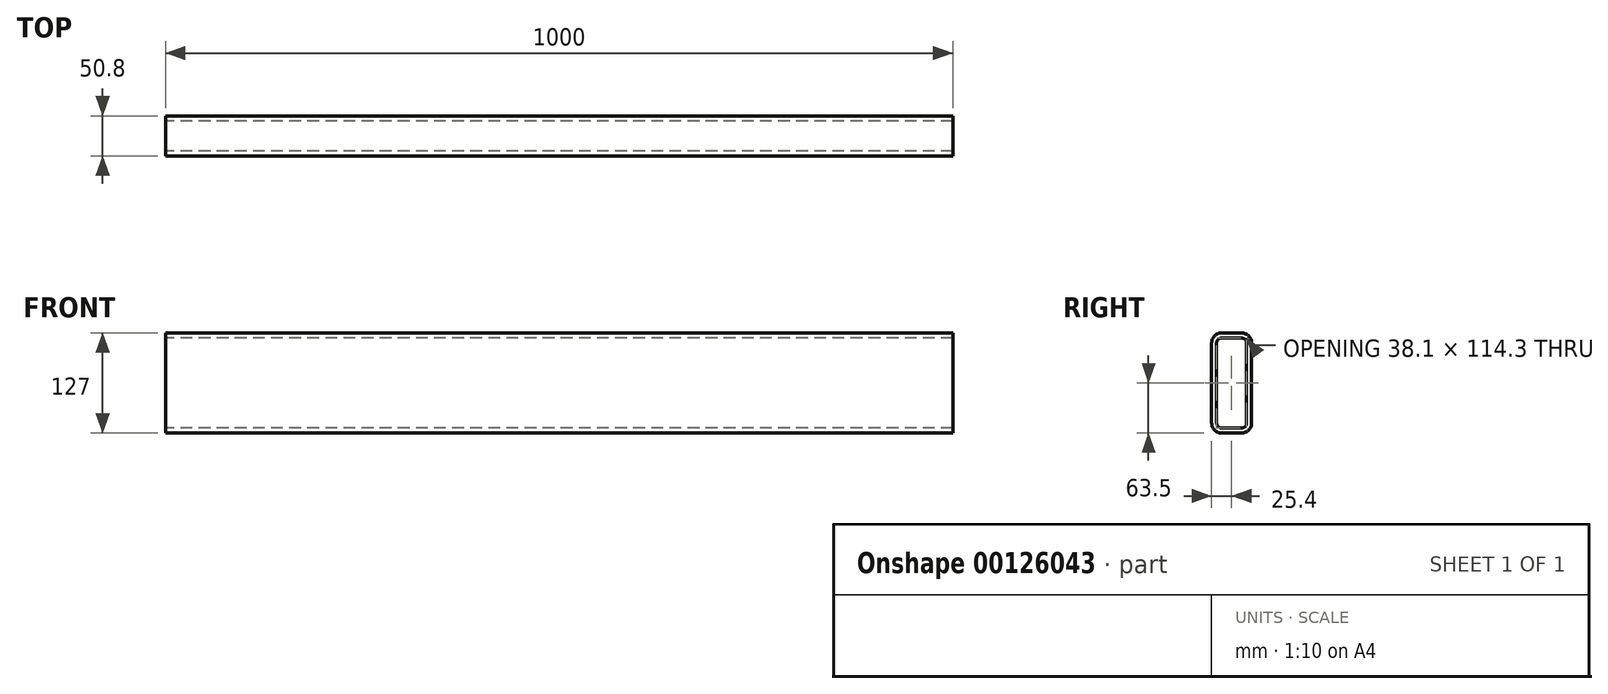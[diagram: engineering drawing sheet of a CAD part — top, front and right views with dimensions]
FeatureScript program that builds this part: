
annotation { "Feature Type Name" : "Feature", "Feature Type Description" : "" }
export const myFeature = defineFeature(function(context is Context, id is Id, definition is map)
    precondition{}
    {
        {
            var Q0;
            Q0=qCreatedBy(makeId("Right.planeOp"),FACE);
            var sketch = newSketch(context, id + "F2", { "sketchPlane" : qUnion([Q0])});
            skLineSegment(sketch, "E0.bottom", {"start": v(12.7, 63.5) * mm, "end": v(-12.7, 63.5) * mm});
            skLineSegment(sketch, "E0.top", {"start": v(12.7, -63.5) * mm, "end": v(-12.7, -63.5) * mm});
            skLineSegment(sketch, "E0.left", {"start": v(25.4, 50.8) * mm, "end": v(25.4, -50.8) * mm});
            skLineSegment(sketch, "E0.right", {"start": v(-25.4, 50.8) * mm, "end": v(-25.4, -50.8) * mm});
            skPoint(sketch, "E0.middle", {"position": v(0, 0) * mm});
            skPoint(sketch, "E1.visualSharp", {"position": v(-25.4, 63.5) * mm});
            skArc(sketch, "E1.filletArc", {"start": v(-12.7, 63.5) * mm, "mid": v(-21.68, 59.78) * mm, "end": v(-25.4, 50.8) * mm});
            skPoint(sketch, "E2.visualSharp", {"position": v(25.4, 63.5) * mm});
            skArc(sketch, "E2.filletArc", {"start": v(25.4, 50.8) * mm, "mid": v(21.68, 59.78) * mm, "end": v(12.7, 63.5) * mm});
            skPoint(sketch, "E3.visualSharp", {"position": v(25.4, -63.5) * mm});
            skArc(sketch, "E3.filletArc", {"start": v(12.7, -63.5) * mm, "mid": v(21.68, -59.78) * mm, "end": v(25.4, -50.8) * mm});
            skPoint(sketch, "E4.visualSharp", {"position": v(-25.4, -63.5) * mm});
            skArc(sketch, "E4.filletArc", {"start": v(-25.4, -50.8) * mm, "mid": v(-21.68, -59.78) * mm, "end": v(-12.7, -63.5) * mm});
            skLineSegment(sketch, "E5.0", {"start": v(12.7, 57.15) * mm, "end": v(-12.7, 57.15) * mm});
            skArc(sketch, "E6.0", {"start": v(19.05, 50.8) * mm, "mid": v(17.2, 55.3) * mm, "end": v(12.7, 57.15) * mm});
            skLineSegment(sketch, "E7.0", {"start": v(19.05, 50.8) * mm, "end": v(19.05, -50.8) * mm});
            skArc(sketch, "E8.0", {"start": v(-12.7, 57.15) * mm, "mid": v(-17.2, 55.3) * mm, "end": v(-19.05, 50.8) * mm});
            skArc(sketch, "E8.1", {"start": v(12.7, -57.15) * mm, "mid": v(17.2, -55.3) * mm, "end": v(19.05, -50.8) * mm});
            skLineSegment(sketch, "E8.2", {"start": v(12.7, -57.15) * mm, "end": v(-12.7, -57.15) * mm});
            skArc(sketch, "E8.3", {"start": v(-19.05, -50.8) * mm, "mid": v(-17.2, -55.3) * mm, "end": v(-12.7, -57.15) * mm});
            skLineSegment(sketch, "E8.4", {"start": v(-19.05, 50.8) * mm, "end": v(-19.05, -50.8) * mm});
            skSolve(sketch);
        }
        {
            var Q0;
            Q0=makeQuery(id+"F2.imprint","IMPRINT",FACE,{"disambiguationData":[TD([[makeQuery(id+"F2.imprint","IMPRINT",EDGE,{"derivedFrom":sQuery(id+"F2.wireOp",EDGE,"E0.bottom")}),1.0]])]});
            extrude(context, id + "F3", {"entities" : qUnion([Q0]), "endBound" : BoundingType.SYMMETRIC, "depth" : 1000 * mm});
        }
        {
            var Q0;
            Q0=makeQuery(id+"F3.opExtrude","SWEPT_BODY",BODY,{"disambiguationData":[OSD([sQuery(id+"F2.wireOp",EDGE,"E0.bottom"),sQuery(id+"F2.wireOp",EDGE,"E0.top"),sQuery(id+"F2.wireOp",EDGE,"E0.left"),sQuery(id+"F2.wireOp",EDGE,"E0.right"),sQuery(id+"F2.wireOp",EDGE,"E1.filletArc"),sQuery(id+"F2.wireOp",EDGE,"E2.filletArc"),sQuery(id+"F2.wireOp",EDGE,"E3.filletArc"),sQuery(id+"F2.wireOp",EDGE,"E4.filletArc"),sQuery(id+"F2.wireOp",EDGE,"E5.0"),sQuery(id+"F2.wireOp",EDGE,"E6.0"),sQuery(id+"F2.wireOp",EDGE,"E7.0"),sQuery(id+"F2.wireOp",EDGE,"E8.0"),sQuery(id+"F2.wireOp",EDGE,"E8.1"),sQuery(id+"F2.wireOp",EDGE,"E8.2"),sQuery(id+"F2.wireOp",EDGE,"E8.3"),sQuery(id+"F2.wireOp",EDGE,"E8.4")])]});
            transform(context, id + "F0", {"entities" : qUnion([Q0]), "transformType" : TransformType.TRANSLATION_3D, "dx" : 0 * mm, "dy" : 0 * mm, "dz" : 0 * mm, "makeCopy" : true});
        }
        {
            var Q0;
            Q0=makeQuery(id+"F0.opPattern","COPY",BODY,{"derivedFrom":makeQuery(id+"F3.opExtrude","SWEPT_BODY",BODY,{"disambiguationData":[OSD([sQuery(id+"F2.wireOp",EDGE,"E0.bottom"),sQuery(id+"F2.wireOp",EDGE,"E0.top"),sQuery(id+"F2.wireOp",EDGE,"E0.left"),sQuery(id+"F2.wireOp",EDGE,"E0.right"),sQuery(id+"F2.wireOp",EDGE,"E1.filletArc"),sQuery(id+"F2.wireOp",EDGE,"E2.filletArc"),sQuery(id+"F2.wireOp",EDGE,"E3.filletArc"),sQuery(id+"F2.wireOp",EDGE,"E4.filletArc"),sQuery(id+"F2.wireOp",EDGE,"E5.0"),sQuery(id+"F2.wireOp",EDGE,"E6.0"),sQuery(id+"F2.wireOp",EDGE,"E7.0"),sQuery(id+"F2.wireOp",EDGE,"E8.0"),sQuery(id+"F2.wireOp",EDGE,"E8.1"),sQuery(id+"F2.wireOp",EDGE,"E8.2"),sQuery(id+"F2.wireOp",EDGE,"E8.3"),sQuery(id+"F2.wireOp",EDGE,"E8.4")])]}),"instanceName":"1"});
            deleteBodies(context, id + "F1", {"entities" : qUnion([Q0])});
        }
    });
